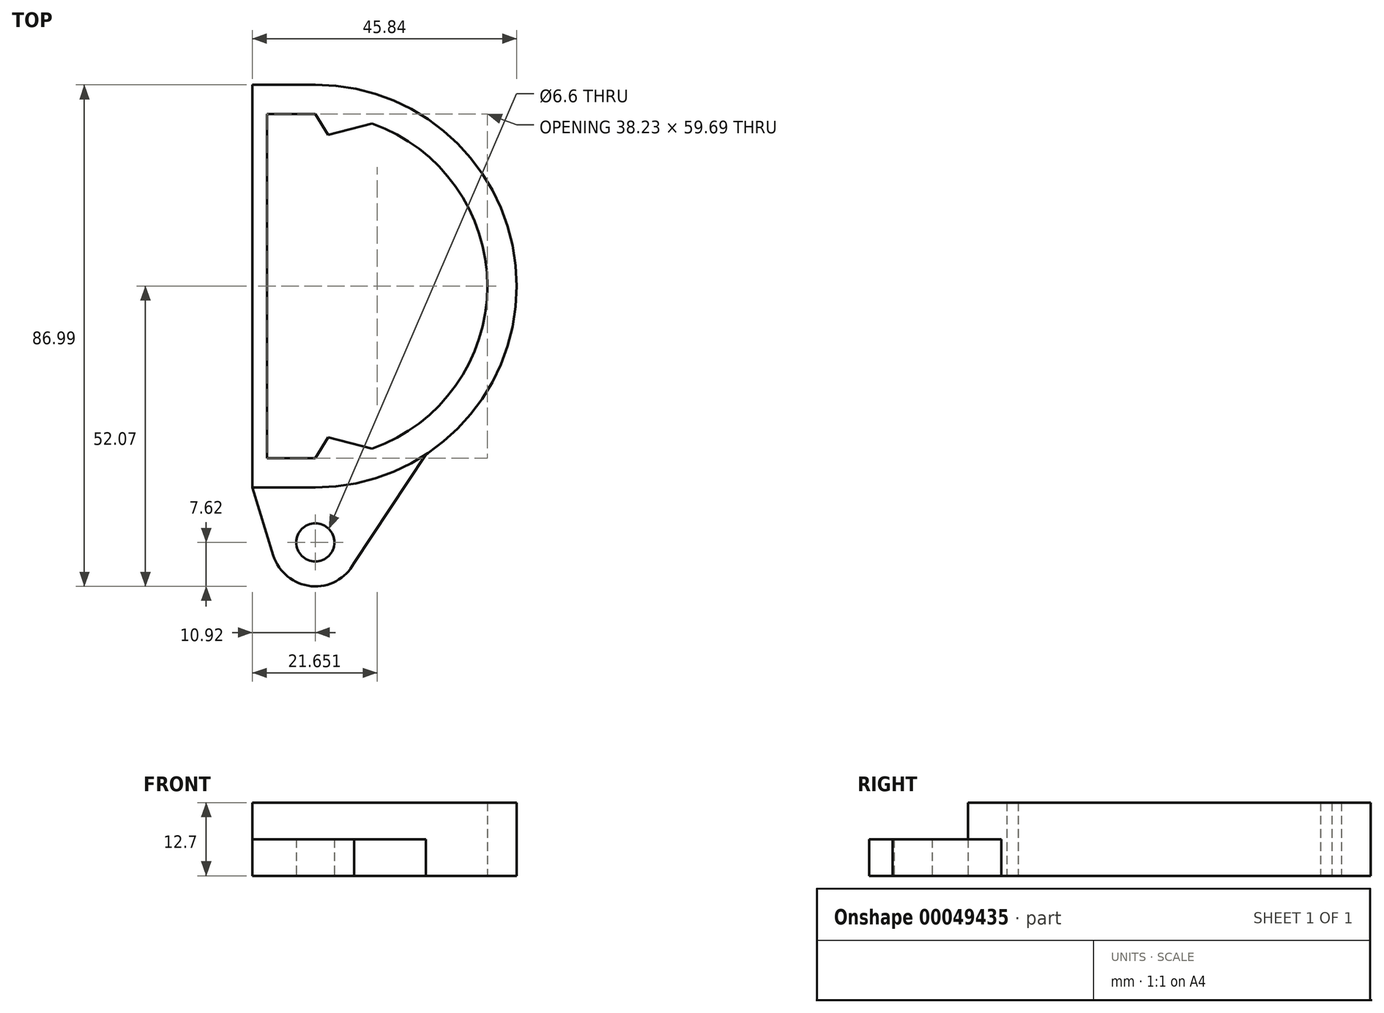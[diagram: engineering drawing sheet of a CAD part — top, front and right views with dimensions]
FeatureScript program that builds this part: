
annotation { "Feature Type Name" : "Feature", "Feature Type Description" : "" }
export const myFeature = defineFeature(function(context is Context, id is Id, definition is map)
    precondition{}
    {
        {
            var Q0;
            Q0=qCreatedBy(makeId("Top.planeOp"),FACE);
            var sketch = newSketch(context, id + "F0", { "sketchPlane" : qUnion([Q0])});
            skArc(sketch, "E0", {"start": v(0, -29.85) * mm, "mid": v(29.85, 0) * mm, "end": v(0, 29.85) * mm});
            skArc(sketch, "E1", {"start": v(0, -34.93) * mm, "mid": v(34.93, 0) * mm, "end": v(0, 34.93) * mm});
            skLineSegment(sketch, "E2", {"start": v(0, 34.93) * mm, "end": v(0, -34.93) * mm, "construction": true});
            skLineSegment(sketch, "E3", {"start": v(0, 34.93) * mm, "end": v(-10.92, 34.93) * mm});
            skLineSegment(sketch, "E4", {"start": v(-10.92, 34.93) * mm, "end": v(-10.92, -34.93) * mm});
            skLineSegment(sketch, "E5", {"start": v(-10.92, -34.93) * mm, "end": v(0, -34.93) * mm});
            skLineSegment(sketch, "E6", {"start": v(0, 29.85) * mm, "end": v(-8.38, 29.85) * mm});
            skLineSegment(sketch, "E7", {"start": v(-8.38, 29.85) * mm, "end": v(-8.38, -29.85) * mm});
            skLineSegment(sketch, "E8", {"start": v(-8.38, -29.85) * mm, "end": v(0, -29.85) * mm});
            skLineSegment(sketch, "E9", {"start": v(0, 29.85) * mm, "end": v(2.24, 26.22) * mm});
            skLineSegment(sketch, "E10", {"start": v(2.24, 26.22) * mm, "end": v(9.84, 28.18) * mm});
            skLineSegment(sketch, "E11", {"start": v(6.33, 0) * mm, "end": v(0, 0) * mm, "construction": true});
            skLineSegment(sketch, "E12.0.MirrorCS", {"start": v(2.24, -26.22) * mm, "end": v(9.84, -28.18) * mm});
            skLineSegment(sketch, "E13.0.MirrorCS", {"start": v(0, -29.85) * mm, "end": v(2.24, -26.22) * mm});
            skSolve(sketch);
        }
        {
            var Q0;
            Q0=makeQuery(id+"F0.imprint","IMPRINT",FACE,{"disambiguationData":[TD([[makeQuery(id+"F0.imprint","IMPRINT",EDGE,{"derivedFrom":sQuery(id+"F0.wireOp",EDGE,"E1")}),1.0]])]});
            var Q1;
            {var subQ1=sQuery(id+"F0.wireOp",EDGE,"E9");Q1=makeQuery(id+"F0.imprint","IMPRINT",FACE,{"disambiguationData":[TD([[makeQuery(id+"F0.imprint","IMPRINT",EDGE,{"derivedFrom":subQ1}),1.0]])]});}
            var Q2;
            {var subQ1=sQuery(id+"F0.wireOp",EDGE,"E12.0.MirrorCS");Q2=makeQuery(id+"F0.imprint","IMPRINT",FACE,{"disambiguationData":[TD([[makeQuery(id+"F0.imprint","IMPRINT",EDGE,{"derivedFrom":subQ1}),-1.0]])]});}
            extrude(context, id + "F1", {"entities" : qUnion([Q0, Q1, Q2]), "depth" : 12.7 * mm});
        }
        {
            var Q0;
            Q0=qCreatedBy(makeId("Top.planeOp"),FACE);
            var sketch = newSketch(context, id + "F2", { "sketchPlane" : qUnion([Q0])});
            skLineSegment(sketch, "E14", {"start": v(0, 0) * mm, "end": v(0, -44.45) * mm, "construction": true});
            skCircle(sketch, "E15", {"center": v(0, -44.45) * mm, "radius": 3.3 * mm});
            skSolve(sketch);
        }
        {
            var Q0;
            Q0=qCreatedBy(makeId("Top.planeOp"),FACE);
            var sketch = newSketch(context, id + "F3", { "sketchPlane" : qUnion([Q0])});
            skCircle(sketch, "E16", {"center": v(0, -44.45) * mm, "radius": 7.62 * mm});
            skLineSegment(sketch, "E17", {"start": v(-10.92, -34.93) * mm, "end": v(-7.28, -46.7) * mm});
            skLineSegment(sketch, "E18", {"start": v(6.73, -48.03) * mm, "end": v(19.2, -29.18) * mm});
            skLineSegment(sketch, "E19", {"start": v(19.2, -29.18) * mm, "end": v(-10.92, -34.93) * mm});
            skSolve(sketch);
        }
        {
            var Q0;
            {var subQ1=sQuery(id+"F3.wireOp",EDGE,"E17");Q0=makeQuery(id+"F3.imprint","IMPRINT",FACE,{"disambiguationData":[TD([[makeQuery(id+"F3.imprint","IMPRINT",EDGE,{"derivedFrom":subQ1}),1.0]])]});}
            var Q1;
            {var subQ0=sQuery(id+"F3.wireOp",EDGE,"E16");var subQ2=makeQuery(id+"F3.imprint","INTERSECT",VERTEX,{"derivedFrom":[subQ0,sQuery(id+"F3.wireOp",EDGE,"E17")]});Q1=makeQuery(id+"F3.imprint","IMPRINT",FACE,{"disambiguationData":[TD([[makeQuery(id+"F3.imprint","IMPRINT",EDGE,{"disambiguationData":[TD([[subQ2,-1.0]])],"derivedFrom":subQ0}),1.0]])]});}
            extrude(context, id + "F4", {"entities" : qUnion([Q0, Q1]), "operationType" : NewBodyOperationType.ADD, "depth" : 6.35 * mm});
        }
        {
            var Q0;
            Q0=qSketchRegion(id+"F2",true);
            extrude(context, id + "F5", {"entities" : qUnion([Q0]), "operationType" : NewBodyOperationType.REMOVE, "depth" : 6.35 * mm});
        }
    });
